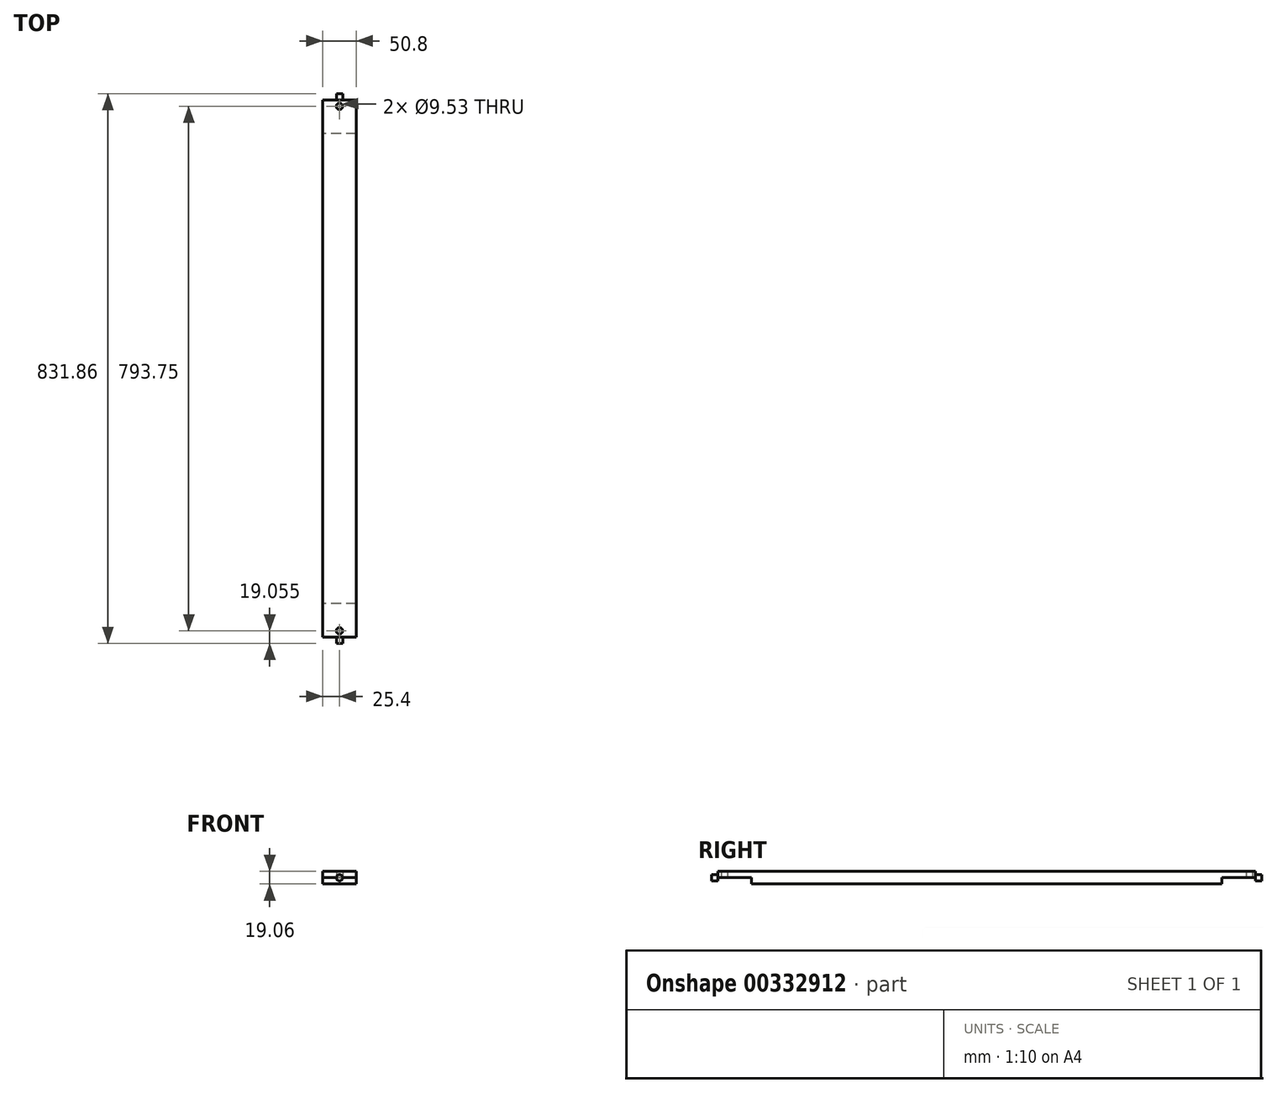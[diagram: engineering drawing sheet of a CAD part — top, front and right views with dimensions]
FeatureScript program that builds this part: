
annotation { "Feature Type Name" : "Feature", "Feature Type Description" : "" }
export const myFeature = defineFeature(function(context is Context, id is Id, definition is map)
    precondition{}
    {
        {
            var Q0;
            Q0=qCreatedBy(makeId("Right.planeOp"),FACE);
            var sketch = newSketch(context, id + "F0", { "sketchPlane" : qUnion([Q0])});
            skLineSegment(sketch, "E0.bottom", {"start": v(-355.6, -9.53) * mm, "end": v(355.6, -9.52) * mm});
            skLineSegment(sketch, "E0.top", {"start": v(-406.4, 9.52) * mm, "end": v(406.4, 9.53) * mm});
            skLineSegment(sketch, "E0.left", {"start": v(-406.4, 0) * mm, "end": v(-406.4, 9.52) * mm});
            skLineSegment(sketch, "E0.right", {"start": v(406.4, 0) * mm, "end": v(406.4, 9.53) * mm});
            skPoint(sketch, "E0.middle", {"position": v(0, 0) * mm});
            skLineSegment(sketch, "E1.bottom", {"start": v(-355.6, 0) * mm, "end": v(-406.4, 0) * mm});
            skLineSegment(sketch, "E1.left", {"start": v(-355.6, 0) * mm, "end": v(-355.6, -9.53) * mm});
            skLineSegment(sketch, "E2.bottom", {"start": v(406.4, 0) * mm, "end": v(355.6, 0) * mm});
            skLineSegment(sketch, "E2.right", {"start": v(355.6, 0) * mm, "end": v(355.6, -9.52) * mm});
            skSolve(sketch);
        }
        {
            var Q0;
            Q0=qSketchRegion(id+"F0",true);
            extrude(context, id + "F1", {"entities" : qUnion([Q0]), "depth" : 50.8 * mm});
        }
        {
            var Q0;
            Q0=makeQuery(id+"F1.opExtrude","SWEPT_FACE",FACE,{"disambiguationData":[OSD([sQuery(id+"F0.wireOp",EDGE,"E0.bottom")])]});
            var sketch = newSketch(context, id + "F2", { "sketchPlane" : qUnion([Q0])});
            skCircle(sketch, "E3", {"center": v(25.4, -396.88) * mm, "radius": 4.76 * mm});
            skCircle(sketch, "E4", {"center": v(25.4, 396.88) * mm, "radius": 4.76 * mm});
            skSolve(sketch);
        }
        {
            var Q0;
            Q0=qSketchRegion(id+"F2",true);
            extrude(context, id + "F3", {"entities" : qUnion([Q0]), "operationType" : NewBodyOperationType.REMOVE, "oppositeDirection" : true, "depth" : 25.4 * mm});
        }
        {
            var Q0;
            Q0=qCreatedBy(makeId("Front.planeOp"),FACE);
            cPlane(context, id + "F4", {"entities" : qUnion([Q0]), "cplaneType" : CPlaneType.OFFSET, "offset" : 406.4 * mm, "width" : 152.4 * mm, "height" : 152.4 * mm});
        }
        {
            var Q0;
            Q0=qCreatedBy(makeId("Front.planeOp"),FACE);
            cPlane(context, id + "F5", {"entities" : qUnion([Q0]), "cplaneType" : CPlaneType.OFFSET, "offset" : 406.4 * mm, "oppositeDirection" : true, "width" : 152.4 * mm, "height" : 152.4 * mm});
        }
        {
            var Q0;
            Q0=qCreatedBy(id+"F4.planeOp",FACE);
            var sketch = newSketch(context, id + "F6", { "sketchPlane" : qUnion([Q0])});
            skCircle(sketch, "E5", {"center": v(25.4, 0) * mm, "radius": 4.76 * mm});
            skSolve(sketch);
        }
        {
            var Q0;
            Q0=qCreatedBy(id+"F5.planeOp",FACE);
            var sketch = newSketch(context, id + "F7", { "sketchPlane" : qUnion([Q0])});
            skCircle(sketch, "E6", {"center": v(25.4, 0) * mm, "radius": 4.76 * mm});
            skSolve(sketch);
        }
        {
            var Q0;
            Q0 = qSketchRegion(id + "F6", true);
            extrude(context, id + "F8", {"entities" : qUnion([Q0]), "depth" : 9.52 * mm});
        }
        {
            var Q0;
            Q0 = qSketchRegion(id + "F7", true);
            extrude(context, id + "F9", {"entities" : qUnion([Q0]), "operationType" : NewBodyOperationType.ADD, "oppositeDirection" : true, "depth" : 9.52 * mm});
        }
    });
